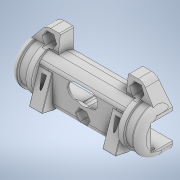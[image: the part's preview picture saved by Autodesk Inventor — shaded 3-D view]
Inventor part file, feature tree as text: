
AUTODESK INVENTOR PART (.ipt)
format: ipt  version: 2022.3 (Build 263350000, 350)  size: 1,877,504 bytes
history: native  units: mm
features: extrude x61, projected_geometry x60, sketch x41, fillet x6, mirror x3, plane x2
ambient origin geometry x8: Origin, YZ Plane, XZ Plane, XY Plane, X Axis, Y Axis, Z Axis, Center Point
bodies: Solid1 (feature_tree)
feature tree (173):
  extrude  "Extrusion1"  Depth=0.6mm
  extrude  "Extrusion2"  Depth=5.1mm
  extrude  "Extrusion3"  Depth=11.5mm TaperAngle=0.0deg
  extrude  "Extrusion4"  Depth=1.0mm
  extrude  "Extrusion5"  Depth=2.5mm TaperAngle=0.0deg
  mirror  "Mirror1"
  extrude  "Extrusion6"  Depth=30.0mm TaperAngle=0.0deg
  extrude  "Extrusion7"  Depth=3.5mm
  extrude  "Extrusion8"  Depth=37.5mm
  extrude  "Extrusion9"  Depth=1.5mm
  extrude  "Extrusion10"  Depth=4.0mm TaperAngle=0.0deg
  fillet  "Fillet1"  Radius=2.75mm
  extrude  "Extrusion11"  Depth=2.7mm
  sketch  "Sketch13"  dims[d37=2.0mm d38=0.0mm d39=3.0mm d40=0.0mm]
  extrude  "Extrusion12"  Depth=3.0mm TaperAngle=0.0deg
  extrude  "Extrusion13"  Depth=0.5mm
  extrude  "Extrusion14"  Depth=5.0mm
  extrude  "Extrusion15"  Depth=2.0mm TaperAngle=0.0deg
  extrude  "Extrusion16"  Depth=5.0mm
  extrude  "Extrusion17"  Depth=1.0mm
  extrude  "Extrusion18"  Depth=14.25mm TaperAngle=0.0deg
  sketch  "Sketch14"  dims[d41=7.0mm d42=0.0mm d43=0.5mm]
  extrude  "Extrusion19"  Depth=14.25mm TaperAngle=0.0deg
  extrude  "Extrusion20"  Depth=14.25mm TaperAngle=0.0deg
  plane  "Work Plane1"
  extrude  "Extrusion21"  Depth=2.5mm TaperAngle=0.0deg
  extrude  "Extrusion22"  Depth=4.0mm TaperAngle=0.0deg
  sketch  "Sketch17"  dims[d49=30.4mm d52=5.0mm]
  extrude  "Extrusion23"  Depth=14.25mm TaperAngle=0.0deg
  extrude  "Extrusion24"  Depth=14.25mm TaperAngle=0.0deg
  extrude  "Extrusion25"  Depth=14.25mm TaperAngle=0.0deg
  fillet  "Fillet3"  Radius=0.5mm
  extrude  "Extrusion26"  Depth=10.0mm TaperAngle=0.0deg
  extrude  "Extrusion27"  TaperAngle=0.0deg  [1 undecoded]
  extrude  "Extrusion28"  TaperAngle=0.0deg  [1 undecoded]
  extrude  "Extrusion29"  Depth=3.0mm TaperAngle=0.0deg
  extrude  "Extrusion30"  TaperAngle=0.0deg  [1 undecoded]
  sketch  "Sketch24"  dims[d75=2.5mm d76=0.0mm d77=14.25mm d78=0.0mm]
  extrude  "Extrusion31"  Depth=10.0mm TaperAngle=0.0deg
  extrude  "Extrusion32"  Depth=10.0mm TaperAngle=0.0deg
  sketch  "Sketch25"  dims[d79=14.25mm d80=0.0mm d82=14.25mm d83=0.0mm]
  extrude  "Extrusion33"  Depth=7.5mm TaperAngle=0.0deg
  extrude  "Extrusion34"  TaperAngle=0.0deg  [1 undecoded]
  extrude  "Extrusion35"  Depth=22.0mm TaperAngle=0.0deg
  extrude  "Extrusion36"  Depth=10.0mm TaperAngle=0.0deg
  sketch  "Sketch26"  dims[d84=2.0mm d85=14.25mm d86=0.0mm d87=0.5mm]
  extrude  "Extrusion37"  Depth=10.0mm TaperAngle=0.0deg
  extrude  "Extrusion38"  Depth=4.0mm TaperAngle=0.0deg
  extrude  "Extrusion39"  Depth=29.237756mm
  extrude  "Extrusion40"  Depth=6.0mm TaperAngle=0.0deg
  mirror  "Mirror2"
  extrude  "Extrusion41"  Depth=10.0mm
  fillet  "Fillet4"  Radius=13.0mm
  extrude  "Extrusion42"  Depth=10.0mm
  extrude  "Extrusion43"  Depth=10.0mm
  extrude  "Extrusion44"  TaperAngle=0.0deg  [1 undecoded]
  sketch  "Sketch34"  dims[d113=10.0mm d114=0.0mm d115=1.0mm d116=0.0mm]
  extrude  "Extrusion47"  Depth=10.0mm
  extrude  "Extrusion48"  Depth=10.0mm
  extrude  "Extrusion49"  Depth=10.0mm TaperAngle=0.0deg
  sketch  "Sketch35"  dims[d117=7.5mm d118=0.0mm d119=7.5mm d120=0.0mm]
  extrude  "Extrusion50"  TaperAngle=0.0deg  [1 undecoded]
  extrude  "Extrusion51"  Depth=10.0mm TaperAngle=0.0deg
  extrude  "Extrusion52"  Depth=10.0mm TaperAngle=0.0deg
  extrude  "Extrusion53"  TaperAngle=0.0deg  [1 undecoded]
  sketch  "Sketch38"  dims[d133=10.0mm d134=0.0mm d135=7.375mm d136=0.0mm]
  extrude  "Extrusion54"  Depth=10.0mm
  extrude  "Extrusion55"  Depth=10.0mm
  extrude  "Extrusion56"  Depth=10.0mm
  extrude  "Extrusion57"  Depth=10.0mm TaperAngle=0.0deg
  sketch  "Sketch41"  dims[d145=15.75mm d146=0.0mm d147=29.237756mm]
  extrude  "Extrusion58"  [1 undecoded]
  extrude  "Extrusion59"  [1 undecoded]
  extrude  "Extrusion60"  [1 undecoded]
  sketch  "Sketch42"  dims[d148=5.0mm d149=6.0mm d150=0.0mm]
  extrude  "Extrusion61"  [1 undecoded]
  extrude  "Extrusion62"  [1 undecoded]
  fillet  "Fillet5"  [1 undecoded]
  fillet  "Fillet6"  [1 undecoded]
  fillet  "Fillet7"  [1 undecoded]
  extrude  "Extrusion63"  [1 undecoded]
  mirror  "Mirror3"
  sketch  "Sketch1"  dims[d0=11.5mm d1=0.0mm d2=0.6mm]
  sketch  "Sketch2"  dims[d3=0.7mm d4=5.1mm]
  projected_geometry  "Projected Loop1"
  projected_geometry  "Projected Loop2"
  sketch  "Sketch3"  dims[d5=2.0mm d6=11.5mm d7=0.0mm]
  sketch  "Sketch4"  dims[d8=1.0mm d9=1.0mm]
  sketch  "Sketch6"  dims[d10=1.0mm d11=2.5mm d12=0.0mm]
  projected_geometry  "Projected Loop3"
  sketch  "Sketch7"  dims[d13=0.1mm d14=0.0mm d21=30.0mm d22=0.0mm]
  projected_geometry  "Projected Loop4"
  projected_geometry  "Projected Loop5"
  projected_geometry  "Projected Loop6"
  sketch  "Sketch8"  dims[d23=44.0mm d24=3.5mm]
  projected_geometry  "Projected Loop7"
  projected_geometry  "Projected Loop8"
  sketch  "Sketch9"  dims[d25=3.0mm d27=37.5mm]
  projected_geometry  "Projected Loop9"
  sketch  "Sketch10"  dims[d28=1.5mm d29=1.5mm]
  projected_geometry  "Projected Loop10"
  sketch  "Sketch11"  dims[d30=3.0mm d31=4.0mm d32=0.0mm d33=2.75mm d34=0.0mm]
  projected_geometry  "Projected Loop11"
  sketch  "Sketch12"  dims[d35=2.7mm d36=2.7mm]
  projected_geometry  "Projected Loop12"
  projected_geometry  "Projected Loop13"
  projected_geometry  "Projected Loop14"
  projected_geometry  "Projected Loop15"
  projected_geometry  "Projected Loop16"
  projected_geometry  "Projected Loop17"
  projected_geometry  "Projected Loop18"
  sketch  "Sketch15"  dims[d44=31.0mm d45=5.0mm]
  sketch  "Sketch16"  dims[d46=3.0mm d47=2.0mm d48=0.0mm]
  projected_geometry  "Projected Loop19"
  projected_geometry  "Projected Loop20"
  projected_geometry  "Projected Loop21"
  projected_geometry  "Projected Loop22"
  sketch  "Sketch18"  dims[d53=2.0mm d54=1.0mm]
  projected_geometry  "Projected Loop23"
  sketch  "Sketch19"  dims[d55=15.0mm d56=0.0mm d57=14.25mm d58=0.0mm]
  projected_geometry  "Projected Loop24"
  projected_geometry  "Projected Loop25"
  sketch  "Sketch20"  dims[d59=14.25mm d60=0.0mm d61=14.25mm d62=0.0mm]
  projected_geometry  "Projected Loop26"
  sketch  "Sketch21"  dims[d63=14.25mm d64=0.0mm d65=14.25mm d66=0.0mm]
  projected_geometry  "Projected Loop27"
  projected_geometry  "Projected Loop28"
  sketch  "Sketch22"  dims[d67=2.5mm d68=0.0mm d69=2.5mm d70=0.0mm]
  projected_geometry  "Projected Loop29"
  sketch  "Sketch23"  dims[d71=2.5mm d72=0.0mm d73=4.0mm d74=0.0mm]
  projected_geometry  "Projected Loop30"
  projected_geometry  "Projected Loop31"
  projected_geometry  "Projected Loop32"
  projected_geometry  "Projected Loop33"
  projected_geometry  "Projected Loop34"
  projected_geometry  "Projected Loop35"
  projected_geometry  "Projected Loop36"
  sketch  "Sketch27"  dims[d88=0.0mm d89=0.0mm d90=10.0mm d91=0.0mm]
  projected_geometry  "Projected Loop37"
  sketch  "Sketch28"  dims[d92=0.0mm d93=0.0mm d94=0.0mm d95=0.0mm]
  projected_geometry  "Projected Loop38"
  plane  "Work Plane2"
  sketch  "Sketch29"  dims[d96=1.0mm d97=0.0mm d98=0.0mm d99=0.0mm]
  projected_geometry  "Projected Loop39"
  sketch  "Sketch30"  dims[d100=8.0mm d101=0.0mm d102=3.0mm d103=0.0mm]
  projected_geometry  "Projected Loop40"
  projected_geometry  "Projected Loop41"
  sketch  "Sketch31"  dims[d104=1.75mm d105=2.25mm d106=0.0mm d107=0.0mm d108=0.0mm d109=0.0mm]
  projected_geometry  "Projected Loop42"
  projected_geometry  "Projected Loop43"
  sketch  "Sketch32"  dims[d110=3.5mm d111=10.0mm d112=0.0mm]
  projected_geometry  "Projected Loop45"
  projected_geometry  "Projected Loop46"
  projected_geometry  "Projected Loop47"
  projected_geometry  "Projected Loop48"
  projected_geometry  "Projected Loop49"
  sketch  "Sketch36"  dims[d121=0.2mm d122=0.0mm d123=0.0mm]
  projected_geometry  "Projected Loop50"
  sketch  "Sketch37"  dims[d124=6.0mm d125=0.0mm d126=22.0mm d127=0.0mm]
  projected_geometry  "Projected Loop51"
  projected_geometry  "Projected Loop52"
  projected_geometry  "Projected Loop53"
  sketch  "Sketch39"  dims[d137=3.375mm d138=0.0mm d139=10.0mm d140=0.0mm]
  projected_geometry  "Projected Loop54"
  sketch  "Sketch40"  dims[d141=5.0mm d142=0.0mm d143=4.0mm d144=0.0mm]
  projected_geometry  "Projected Loop55"
  projected_geometry  "Projected Loop56"
  projected_geometry  "Projected Loop57"
  projected_geometry  "Projected Loop58"
  projected_geometry  "Projected Loop59"
  projected_geometry  "Projected Loop60"
  sketch  "Sketch43"  dims[d151=8.0mm d152=0.0mm d153=2.5mm d154=13.0mm d155=0.0mm d156=6.0mm d157=7.0mm d158=0.0mm d159=0.0mm d160=3.0mm d161=2.8mm d162=11.5mm d163=0.0mm d164=0.0mm d165=0.0mm d166=7.8mm d167=0.0mm d168=10.0mm d169=0.0mm d170=0.0mm d171=0.0mm d172=3.0mm d173=0.2mm d174=1.0mm d175=0.25mm d176=0.0mm]
  projected_geometry  "Projected Loop61"
note: 16 required parameter values undecoded (feature->parameter linkage not recoverable at this tier; creation-order binding heuristic only, values carry confidence <= 0.55)
